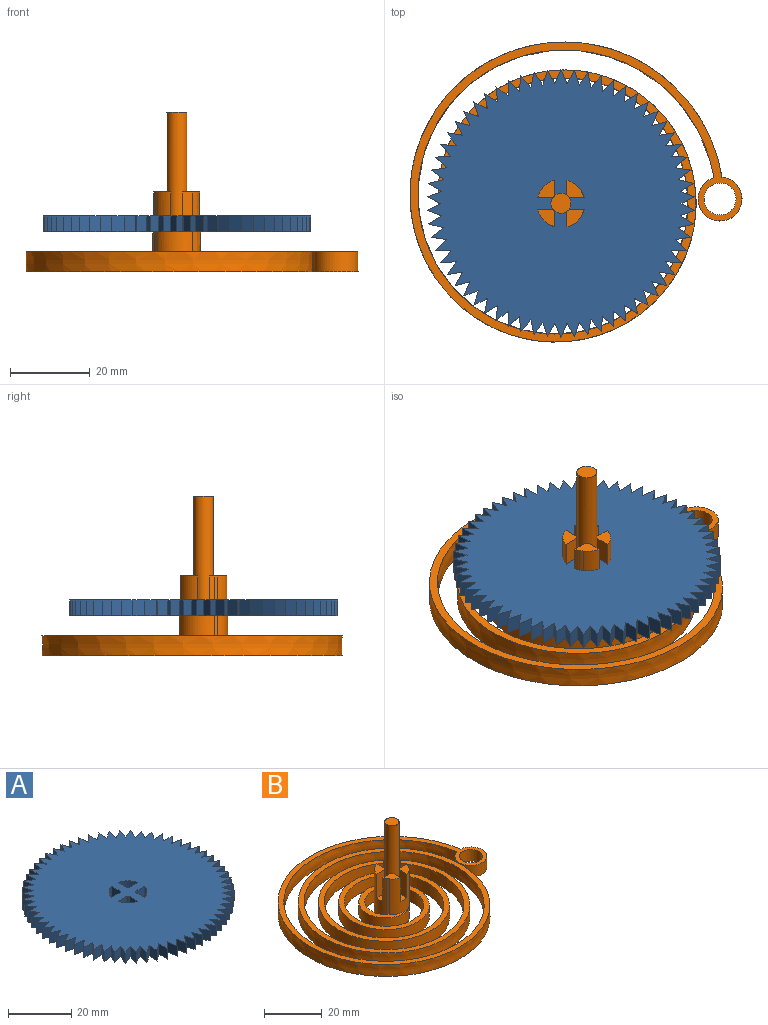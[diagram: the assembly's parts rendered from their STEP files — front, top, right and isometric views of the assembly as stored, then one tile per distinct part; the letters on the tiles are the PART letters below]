
ASSEMBLY  parts=2 mates=1
PART A: 204 faces, bbox 66.9x67x4 mm
  f0: plane 67x66.91mm, normal (0,0,1), area 3101.5mm2, adj f2,f3,f4,f5,f6,f7,f8,f9
  f1: plane 67x66.91mm, normal (0,0,-1), area 3101.5mm2, adj f2,f3,f4,f5,f6,f7,f8,f9
  f2: plane 4x3.61mm, normal (0.34,0.94,0), area 15.4mm2, adj f0,f1,f3,f187
  f3: cylinder r=30mm len=4mm, axis (0,0,-1), area 0.2mm2, adj f0,f1,f2,f4
  f4: plane 4x3.27mm, normal (0.53,-0.85,0), area 15.4mm2, adj f0,f1,f3,f5
  f5: plane 4x3.72mm, normal (0.25,0.97,0), area 15.4mm2, adj f0,f1,f4,f6
  f6: cylinder r=30mm len=4mm, axis (0,0,-1), area 0.2mm2, adj f0,f1,f5,f7
  f7: plane 4x3.05mm, normal (0.61,-0.79,0), area 15.4mm2, adj f0,f1,f6,f8
  f8: plane 4x3.8mm, normal (0.15,0.99,0), area 15.4mm2, adj f0,f1,f7,f9
  f9: cylinder r=30mm len=4mm, axis (0,0,-1), area 0.2mm2, adj f0,f1,f8,f10
  f10: plane 4x2.8mm, normal (0.69,-0.73,0), area 15.4mm2, adj f0,f1,f9,f11
  f11: plane 4x3.84mm, normal (0.05,1,0), area 15.4mm2, adj f0,f1,f10,f12
  f12: cylinder r=30mm len=4mm, axis (0,0,-1), area 0.2mm2, adj f0,f1,f11,f13
  f13: plane 4x2.9mm, normal (0.76,-0.65,0), area 15.4mm2, adj f0,f1,f12,f14
  f14: plane 4x3.84mm, normal (-0.05,1,0), area 15.4mm2, adj f0,f1,f13,f15
  f15: cylinder r=30mm len=4mm, axis (0,0,-1), area 0.2mm2, adj f0,f1,f14,f16
  f16: plane 4x3.14mm, normal (0.82,-0.57,0), area 15.4mm2, adj f0,f1,f15,f17
  f17: plane 4x3.8mm, normal (-0.16,0.99,0), area 15.4mm2, adj f0,f1,f16,f18
  f18: cylinder r=30mm len=4mm, axis (0,0,-1), area 0.2mm2, adj f0,f1,f17,f19
  f19: plane 4x3.35mm, normal (0.87,-0.49,0), area 15.4mm2, adj f0,f1,f18,f20
  f20: plane 4x3.72mm, normal (-0.25,0.97,0), area 15.4mm2, adj f0,f1,f19,f21
  f21: cylinder r=30mm len=4mm, axis (0,0,-1), area 0.2mm2, adj f0,f1,f20,f22
  f22: plane 4x3.52mm, normal (0.92,-0.4,0), area 15.4mm2, adj f0,f1,f21,f23
  f23: plane 4x3.6mm, normal (-0.35,0.94,0), area 15.4mm2, adj f0,f1,f22,f24
  f24: cylinder r=30mm len=4mm, axis (0,0,-1), area 0.2mm2, adj f0,f1,f23,f25
  f25: plane 4x3.66mm, normal (0.95,-0.3,0), area 15.4mm2, adj f0,f1,f24,f26
  f26: plane 4x3.44mm, normal (-0.44,0.9,0), area 15.4mm2, adj f0,f1,f25,f27
  f27: cylinder r=30mm len=4mm, axis (0,0,-1), area 0.2mm2, adj f0,f1,f26,f28
  f28: plane 4x3.76mm, normal (0.98,-0.21,0), area 15.4mm2, adj f0,f1,f27,f29
  f29: plane 4x3.25mm, normal (-0.53,0.85,0), area 15.4mm2, adj f0,f1,f28,f30
  f30: cylinder r=30mm len=4mm, axis (0,0,-1), area 0.2mm2, adj f0,f1,f29,f31
  f31: plane 4x3.82mm, normal (0.99,-0.11,0), area 15.4mm2, adj f0,f1,f30,f32
  f32: plane 4x3.03mm, normal (-0.62,0.79,0), area 15.4mm2, adj f0,f1,f31,f33
  f33: cylinder r=30mm len=4mm, axis (0,0,-1), area 0.2mm2, adj f0,f1,f32,f34
  f34: plane 4x3.84mm, normal (1,0,0), area 15.4mm2, adj f0,f1,f33,f35
  f35: plane 4x2.77mm, normal (-0.69,0.72,0), area 15.4mm2, adj f0,f1,f34,f36
  f36: cylinder r=30mm len=4mm, axis (0,0,-1), area 0.2mm2, adj f0,f1,f35,f37
  f37: plane 4x3.82mm, normal (1,0.1,0), area 15.4mm2, adj f0,f1,f36,f38
  f38: plane 4x2.93mm, normal (-0.76,0.65,0), area 15.4mm2, adj f0,f1,f37,f39
  f39: cylinder r=30mm len=4mm, axis (0,0,-1), area 0.2mm2, adj f0,f1,f38,f40
  f40: plane 4x3.77mm, normal (0.98,0.2,0), area 15.4mm2, adj f0,f1,f39,f41
  f41: plane 4x3.16mm, normal (-0.82,0.57,0), area 15.4mm2, adj f0,f1,f40,f42
  f42: cylinder r=30mm len=4mm, axis (0,0,-1), area 0.2mm2, adj f0,f1,f41,f43
  f43: plane 4x3.67mm, normal (0.96,0.3,0), area 15.4mm2, adj f0,f1,f42,f44
  f44: plane 4x3.37mm, normal (-0.88,0.48,0), area 15.4mm2, adj f0,f1,f43,f45
  f45: cylinder r=30mm len=4mm, axis (0,0,-1), area 0.2mm2, adj f0,f1,f44,f46
  f46: plane 4x3.54mm, normal (0.92,0.39,0), area 15.4mm2, adj f0,f1,f45,f47
  f47: plane 4x3.54mm, normal (-0.92,0.39,0), area 15.4mm2, adj f0,f1,f46,f48
  f48: cylinder r=30mm len=4mm, axis (0,0,-1), area 0.2mm2, adj f0,f1,f47,f49
  f49: plane 4x3.37mm, normal (0.88,0.48,0), area 15.4mm2, adj f0,f1,f48,f50
  f50: plane 4x3.67mm, normal (-0.96,0.3,0), area 15.4mm2, adj f0,f1,f49,f51
  f51: cylinder r=30mm len=4mm, axis (0,0,-1), area 0.2mm2, adj f0,f1,f50,f52
  f52: plane 4x3.16mm, normal (0.82,0.57,0), area 15.4mm2, adj f0,f1,f51,f53
  f53: plane 4x3.77mm, normal (-0.98,0.2,0), area 15.4mm2, adj f0,f1,f52,f54
  f54: cylinder r=30mm len=4mm, axis (0,0,-1), area 0.2mm2, adj f0,f1,f53,f55
  f55: plane 4x2.93mm, normal (0.76,0.65,0), area 15.4mm2, adj f0,f1,f54,f56
  f56: plane 4x3.82mm, normal (-1,0.1,0), area 15.4mm2, adj f0,f1,f55,f57
  f57: cylinder r=30mm len=4mm, axis (0,0,-1), area 0.2mm2, adj f0,f1,f56,f58
  f58: plane 4x2.77mm, normal (0.69,0.72,0), area 15.4mm2, adj f0,f1,f57,f59
  f59: plane 4x3.84mm, normal (-1,0,0), area 15.4mm2, adj f0,f1,f58,f60
  f60: cylinder r=30mm len=4mm, axis (0,0,-1), area 0.2mm2, adj f0,f1,f59,f61
  f61: plane 4x3.03mm, normal (0.62,0.79,0), area 15.4mm2, adj f0,f1,f60,f62
  f62: plane 4x3.82mm, normal (-0.99,-0.11,0), area 15.4mm2, adj f0,f1,f61,f63
  f63: cylinder r=30mm len=4mm, axis (0,0,-1), area 0.2mm2, adj f0,f1,f62,f64
  f64: plane 4x3.25mm, normal (0.53,0.85,0), area 15.4mm2, adj f0,f1,f63,f65
  f65: plane 4x3.76mm, normal (-0.98,-0.21,0), area 15.4mm2, adj f0,f1,f64,f66
  f66: cylinder r=30mm len=4mm, axis (0,0,-1), area 0.2mm2, adj f0,f1,f65,f67
  f67: plane 4x3.44mm, normal (0.44,0.9,0), area 15.4mm2, adj f0,f1,f66,f68
  f68: plane 4x3.66mm, normal (-0.95,-0.3,0), area 15.4mm2, adj f0,f1,f67,f69
  f69: cylinder r=30mm len=4mm, axis (0,0,-1), area 0.2mm2, adj f0,f1,f68,f70
  f70: plane 4x3.6mm, normal (0.35,0.94,0), area 15.4mm2, adj f0,f1,f69,f71
  f71: plane 4x3.52mm, normal (-0.92,-0.4,0), area 15.4mm2, adj f0,f1,f70,f72
  f72: cylinder r=30mm len=4mm, axis (0,0,-1), area 0.2mm2, adj f0,f1,f71,f73
  f73: plane 4x3.72mm, normal (0.25,0.97,0), area 15.4mm2, adj f0,f1,f72,f74
  f74: plane 4x3.35mm, normal (-0.87,-0.49,0), area 15.4mm2, adj f0,f1,f73,f75
  f75: cylinder r=30mm len=4mm, axis (0,0,-1), area 0.2mm2, adj f0,f1,f74,f76
  f76: plane 4x3.8mm, normal (0.16,0.99,0), area 15.4mm2, adj f0,f1,f75,f77
  f77: plane 4x3.14mm, normal (-0.82,-0.57,0), area 15.4mm2, adj f0,f1,f76,f78
  f78: cylinder r=30mm len=4mm, axis (0,0,-1), area 0.2mm2, adj f0,f1,f77,f79
  f79: plane 4x3.84mm, normal (0.05,1,0), area 15.4mm2, adj f0,f1,f78,f80
  f80: plane 4x2.9mm, normal (-0.76,-0.65,0), area 15.4mm2, adj f0,f1,f79,f81
  f81: cylinder r=30mm len=4mm, axis (0,0,-1), area 0.2mm2, adj f0,f1,f80,f82
  f82: plane 4x3.84mm, normal (-0.05,1,0), area 15.4mm2, adj f0,f1,f81,f83
  f83: plane 4x2.8mm, normal (-0.69,-0.73,0), area 15.4mm2, adj f0,f1,f82,f84
  f84: cylinder r=30mm len=4mm, axis (0,0,-1), area 0.2mm2, adj f0,f1,f83,f85
  f85: plane 4x3.8mm, normal (-0.15,0.99,0), area 15.4mm2, adj f0,f1,f84,f86
  f86: plane 4x3.05mm, normal (-0.61,-0.79,0), area 15.4mm2, adj f0,f1,f85,f87
  f87: cylinder r=30mm len=4mm, axis (0,0,-1), area 0.2mm2, adj f0,f1,f86,f88
  f88: plane 4x3.72mm, normal (-0.25,0.97,0), area 15.4mm2, adj f0,f1,f87,f89
  f89: plane 4x3.27mm, normal (-0.53,-0.85,0), area 15.4mm2, adj f0,f1,f88,f90
  f90: cylinder r=30mm len=4mm, axis (0,0,-1), area 0.2mm2, adj f0,f1,f89,f91
  f91: plane 4x3.61mm, normal (-0.34,0.94,0), area 15.4mm2, adj f0,f1,f90,f92
  f92: plane 4x3.46mm, normal (-0.44,-0.9,0), area 15.4mm2, adj f0,f1,f91,f93
  f93: cylinder r=30mm len=4mm, axis (0,0,-1), area 0.2mm2, adj f0,f1,f92,f94
  f94: plane 4x3.46mm, normal (-0.44,0.9,0), area 15.4mm2, adj f0,f1,f93,f95
  f95: plane 4x3.61mm, normal (-0.34,-0.94,0), area 15.4mm2, adj f0,f1,f94,f96
  f96: cylinder r=30mm len=4mm, axis (0,0,-1), area 0.2mm2, adj f0,f1,f95,f97
  f97: plane 4x3.27mm, normal (-0.53,0.85,0), area 15.4mm2, adj f0,f1,f96,f98
  f98: plane 4x3.72mm, normal (-0.25,-0.97,0), area 15.4mm2, adj f0,f1,f97,f99
  f99: cylinder r=30mm len=4mm, axis (0,0,-1), area 0.2mm2, adj f0,f1,f98,f100
  f100: plane 4x3.05mm, normal (-0.61,0.79,0), area 15.4mm2, adj f0,f1,f99,f101
  f101: plane 4x3.8mm, normal (-0.15,-0.99,0), area 15.4mm2, adj f0,f1,f100,f102
  f102: cylinder r=30mm len=4mm, axis (0,0,-1), area 0.2mm2, adj f0,f1,f101,f103
  f103: plane 4x2.8mm, normal (-0.69,0.73,0), area 15.4mm2, adj f0,f1,f102,f104
  f104: plane 4x3.84mm, normal (-0.05,-1,0), area 15.4mm2, adj f0,f1,f103,f105
  f105: cylinder r=30mm len=4mm, axis (0,0,-1), area 0.2mm2, adj f0,f1,f104,f106
  f106: plane 4x2.9mm, normal (-0.76,0.65,0), area 15.4mm2, adj f0,f1,f105,f107
  f107: plane 4x3.84mm, normal (0.05,-1,0), area 15.4mm2, adj f0,f1,f106,f108
  f108: cylinder r=30mm len=4mm, axis (0,0,-1), area 0.2mm2, adj f0,f1,f107,f109
  f109: plane 4x3.14mm, normal (-0.82,0.57,0), area 15.4mm2, adj f0,f1,f108,f110
  f110: plane 4x3.8mm, normal (0.16,-0.99,0), area 15.4mm2, adj f0,f1,f109,f111
  f111: cylinder r=30mm len=4mm, axis (0,0,-1), area 0.2mm2, adj f0,f1,f110,f112
  f112: plane 4x3.35mm, normal (-0.87,0.49,0), area 15.4mm2, adj f0,f1,f111,f113
  f113: plane 4x3.72mm, normal (0.25,-0.97,0), area 15.4mm2, adj f0,f1,f112,f114
  f114: cylinder r=30mm len=4mm, axis (0,0,-1), area 0.2mm2, adj f0,f1,f113,f115
  f115: plane 4x3.52mm, normal (-0.92,0.4,0), area 15.4mm2, adj f0,f1,f114,f116
  f116: plane 4x3.6mm, normal (0.35,-0.94,0), area 15.4mm2, adj f0,f1,f115,f117
  f117: cylinder r=30mm len=4mm, axis (0,0,-1), area 0.2mm2, adj f0,f1,f116,f118
  f118: plane 4x3.66mm, normal (-0.95,0.3,0), area 15.4mm2, adj f0,f1,f117,f119
  f119: plane 4x3.44mm, normal (0.44,-0.9,0), area 15.4mm2, adj f0,f1,f118,f120
  f120: cylinder r=30mm len=4mm, axis (0,0,-1), area 0.2mm2, adj f0,f1,f119,f121
  f121: plane 4x3.76mm, normal (-0.98,0.21,0), area 15.4mm2, adj f0,f1,f120,f122
  f122: plane 4x3.25mm, normal (0.53,-0.85,0), area 15.4mm2, adj f0,f1,f121,f123
  f123: cylinder r=30mm len=4mm, axis (0,0,-1), area 0.2mm2, adj f0,f1,f122,f124
  f124: plane 4x3.82mm, normal (-0.99,0.11,0), area 15.4mm2, adj f0,f1,f123,f125
  f125: plane 4x3.03mm, normal (0.62,-0.79,0), area 15.4mm2, adj f0,f1,f124,f126
  f126: cylinder r=30mm len=4mm, axis (0,0,-1), area 0.2mm2, adj f0,f1,f125,f127
  f127: plane 4x3.84mm, normal (-1,0,0), area 15.4mm2, adj f0,f1,f126,f128
  f128: plane 4x2.77mm, normal (0.69,-0.72,0), area 15.4mm2, adj f0,f1,f127,f129
  f129: cylinder r=30mm len=4mm, axis (0,0,-1), area 0.2mm2, adj f0,f1,f128,f130
  f130: plane 4x3.82mm, normal (-1,-0.1,0), area 15.4mm2, adj f0,f1,f129,f131
  f131: plane 4x2.93mm, normal (0.76,-0.65,0), area 15.4mm2, adj f0,f1,f130,f132
  f132: cylinder r=30mm len=4mm, axis (0,0,-1), area 0.2mm2, adj f0,f1,f131,f133
  f133: plane 4x3.77mm, normal (-0.98,-0.2,0), area 15.4mm2, adj f0,f1,f132,f134
  f134: plane 4x3.16mm, normal (0.82,-0.57,0), area 15.4mm2, adj f0,f1,f133,f135
  f135: cylinder r=30mm len=4mm, axis (0,0,-1), area 0.2mm2, adj f0,f1,f134,f136
  f136: plane 4x3.67mm, normal (-0.96,-0.3,0), area 15.4mm2, adj f0,f1,f135,f137
  f137: plane 4x3.37mm, normal (0.88,-0.48,0), area 15.4mm2, adj f0,f1,f136,f138
  f138: cylinder r=30mm len=4mm, axis (0,0,-1), area 0.2mm2, adj f0,f1,f137,f139
  f139: plane 4x3.54mm, normal (-0.92,-0.39,0), area 15.4mm2, adj f0,f1,f138,f140
  f140: plane 4x3.54mm, normal (0.92,-0.39,0), area 15.4mm2, adj f0,f1,f139,f141
  f141: cylinder r=30mm len=4mm, axis (0,0,-1), area 0.2mm2, adj f0,f1,f140,f142
  f142: plane 4x3.37mm, normal (-0.88,-0.48,0), area 15.4mm2, adj f0,f1,f141,f143
  f143: plane 4x3.67mm, normal (0.96,-0.3,0), area 15.4mm2, adj f0,f1,f142,f144
  f144: cylinder r=30mm len=4mm, axis (0,0,-1), area 0.2mm2, adj f0,f1,f143,f145
  f145: plane 4x3.16mm, normal (-0.82,-0.57,0), area 15.4mm2, adj f0,f1,f144,f146
  f146: plane 4x3.77mm, normal (0.98,-0.2,0), area 15.4mm2, adj f0,f1,f145,f147
  f147: cylinder r=30mm len=4mm, axis (0,0,-1), area 0.2mm2, adj f0,f1,f146,f148
  f148: plane 4x2.93mm, normal (-0.76,-0.65,0), area 15.4mm2, adj f0,f1,f147,f149
  f149: plane 4x3.82mm, normal (1,-0.1,0), area 15.4mm2, adj f0,f1,f148,f150
  f150: cylinder r=30mm len=4mm, axis (0,0,-1), area 0.2mm2, adj f0,f1,f149,f151
  f151: plane 4x2.77mm, normal (-0.69,-0.72,0), area 15.4mm2, adj f0,f1,f150,f152
  f152: plane 4x3.84mm, normal (1,0,0), area 15.4mm2, adj f0,f1,f151,f153
  f153: cylinder r=30mm len=4mm, axis (0,0,-1), area 0.2mm2, adj f0,f1,f152,f154
  f154: plane 4x3.03mm, normal (-0.62,-0.79,0), area 15.4mm2, adj f0,f1,f153,f155
  f155: plane 4x3.82mm, normal (0.99,0.11,0), area 15.4mm2, adj f0,f1,f154,f156
  f156: cylinder r=30mm len=4mm, axis (0,0,-1), area 0.2mm2, adj f0,f1,f155,f157
  f157: plane 4x3.25mm, normal (-0.53,-0.85,0), area 15.4mm2, adj f0,f1,f156,f158
  f158: plane 4x3.76mm, normal (0.98,0.21,0), area 15.4mm2, adj f0,f1,f157,f159
  f159: cylinder r=30mm len=4mm, axis (0,0,-1), area 0.2mm2, adj f0,f1,f158,f160
  f160: plane 4x3.44mm, normal (-0.44,-0.9,0), area 15.4mm2, adj f0,f1,f159,f161
  f161: plane 4x3.66mm, normal (0.95,0.3,0), area 15.4mm2, adj f0,f1,f160,f162
  f162: cylinder r=30mm len=4mm, axis (0,0,-1), area 0.2mm2, adj f0,f1,f161,f163
  f163: plane 4x3.6mm, normal (-0.35,-0.94,0), area 15.4mm2, adj f0,f1,f162,f164
  f164: plane 4x3.52mm, normal (0.92,0.4,0), area 15.4mm2, adj f0,f1,f163,f165
  f165: cylinder r=30mm len=4mm, axis (0,0,-1), area 0.2mm2, adj f0,f1,f164,f166
  f166: plane 4x3.72mm, normal (-0.25,-0.97,0), area 15.4mm2, adj f0,f1,f165,f167
  f167: plane 4x3.35mm, normal (0.87,0.49,0), area 15.4mm2, adj f0,f1,f166,f168
  f168: cylinder r=30mm len=4mm, axis (0,0,-1), area 0.2mm2, adj f0,f1,f167,f169
  f169: plane 4x3.8mm, normal (-0.16,-0.99,0), area 15.4mm2, adj f0,f1,f168,f170
  f170: plane 4x3.14mm, normal (0.82,0.57,0), area 15.4mm2, adj f0,f1,f169,f171
  f171: cylinder r=30mm len=4mm, axis (0,0,-1), area 0.2mm2, adj f0,f1,f170,f172
  f172: plane 4x3.84mm, normal (-0.05,-1,0), area 15.4mm2, adj f0,f1,f171,f173
  f173: plane 4x2.9mm, normal (0.76,0.65,0), area 15.4mm2, adj f0,f1,f172,f174
  f174: cylinder r=30mm len=4mm, axis (0,0,-1), area 0.2mm2, adj f0,f1,f173,f175
  f175: plane 4x3.84mm, normal (0.05,-1,0), area 15.4mm2, adj f0,f1,f174,f176
  f176: plane 4x2.8mm, normal (0.69,0.73,0), area 15.4mm2, adj f0,f1,f175,f177
  f177: cylinder r=30mm len=4mm, axis (0,0,-1), area 0.2mm2, adj f0,f1,f176,f178
  f178: plane 4x3.8mm, normal (0.15,-0.99,0), area 15.4mm2, adj f0,f1,f177,f179
  f179: plane 4x3.05mm, normal (0.61,0.79,0), area 15.4mm2, adj f0,f1,f178,f180
  f180: cylinder r=30mm len=4mm, axis (0,0,-1), area 0.2mm2, adj f0,f1,f179,f181
  f181: plane 4x3.72mm, normal (0.25,-0.97,0), area 15.4mm2, adj f0,f1,f180,f182
  f182: plane 4x3.27mm, normal (0.53,0.85,0), area 15.4mm2, adj f0,f1,f181,f183
  f183: cylinder r=30mm len=4mm, axis (0,0,-1), area 0.2mm2, adj f0,f1,f182,f184
  f184: plane 4x3.61mm, normal (0.34,-0.94,0), area 15.4mm2, adj f0,f1,f183,f185
  f185: plane 4x3.46mm, normal (0.44,0.9,0), area 15.4mm2, adj f0,f1,f184,f186
  f186: cylinder r=30mm len=4mm, axis (0,0,-1), area 0.2mm2, adj f0,f1,f185,f187
  f187: plane 4x3.46mm, normal (0.44,-0.9,0), area 15.4mm2, adj f0,f1,f2,f186
  f188: plane 4x3.81mm, normal (0,1,0), area 15.2mm2, adj f0,f1,f189,f191
  f189: cylinder r=2.5mm len=4mm, axis (0,0,1), area 2.8mm2, adj f0,f1,f188,f190
  f190: plane 4x3.81mm, normal (-1,0,0), area 15.2mm2, adj f0,f1,f189,f191
  f191: cylinder r=6mm len=4.31mm, axis (0,0,1), area 25.6mm2, adj f0,f1,f188,f190
  f192: plane 4x3.81mm, normal (0,1,0), area 15.2mm2, adj f0,f1,f193,f195
  f193: cylinder r=6mm len=4.31mm, axis (0,0,1), area 25.6mm2, adj f0,f1,f192,f194
  f194: plane 4x3.81mm, normal (1,0,0), area 15.2mm2, adj f0,f1,f193,f195
  f195: cylinder r=2.5mm len=4mm, axis (0,0,1), area 2.8mm2, adj f0,f1,f192,f194
  f196: plane 4x3.81mm, normal (1,0,0), area 15.2mm2, adj f0,f1,f197,f199
  f197: cylinder r=6mm len=4.31mm, axis (0,0,1), area 25.6mm2, adj f0,f1,f196,f198
  f198: plane 4x3.81mm, normal (0,-1,0), area 15.2mm2, adj f0,f1,f197,f199
  f199: cylinder r=2.5mm len=4mm, axis (0,0,1), area 2.8mm2, adj f0,f1,f196,f198
  f200: plane 4x3.81mm, normal (-1,0,0), area 15.2mm2, adj f0,f1,f201,f203
  f201: cylinder r=2.5mm len=4mm, axis (0,0,1), area 2.8mm2, adj f0,f1,f200,f202
  f202: plane 4x3.81mm, normal (0,-1,0), area 15.2mm2, adj f0,f1,f201,f203
  f203: cylinder r=6mm len=4.31mm, axis (0,0,1), area 25.6mm2, adj f0,f1,f200,f202
PART B: 30 faces, bbox 83.2x75.3x40 mm
  f0: extruded ~77.64x70.27mm, area 3637.6mm2, adj f1,f9,f11,f14
  f1: extruded ~20x6.07mm, area 104.5mm2, adj f0,f3,f4,f6,f11,f21,f22
  f2: cylinder r=6.04mm len=15mm, axis (0,0,-1), area 139.3mm2, adj f4,f5,f7,f10,f18,f19,f27,f28
  f3: cylinder r=6.04mm len=15mm, axis (0,0,-1), area 116.1mm2, adj f1,f5,f6,f8,f9,f24,f25,f26
  f4: cylinder r=5.98mm len=20mm, axis (0,0,1), area 225.4mm2, adj f1,f2,f5,f8,f10,f11,f12,f16
  f5: plane 4.35x4.35mm, normal (0,0,1), area 12.8mm2, adj f2,f3,f4,f8,f15,f26,f28
  f6: plane 4.37x4.21mm, normal (0,0,1), area 12.4mm2, adj f1,f3,f15,f22,f25
  f7: plane 4.35x4.35mm, normal (0,0,1), area 12.8mm2, adj f2,f15,f19,f29
  f8: extruded ~15x0.04mm, area 0.7mm2, adj f3,f4,f5,f12
  f9: plane 83.12x75.18mm, normal (0,0,1), area 1412.2mm2, adj f0,f3,f12,f13,f14
  f10: plane 8.83x5.84mm, normal (0,0,1), area 0.4mm2, adj f2,f4
  f11: plane 83.16x75.25mm, normal (0,0,-1), area 1527.4mm2, adj f0,f1,f4,f12,f13,f14
  f12: extruded ~72.81x68.03mm, area 3293.5mm2, adj f4,f8,f9,f11,f14
  f13: cylinder r=4mm len=8mm, axis (0,0,1), area 125.7mm2, adj f9,f11
  f14: cylinder r=5.5mm len=11mm, axis (0,0,1), area 162.7mm2, adj f0,f9,f11,f12
  f15: cylinder r=2.5mm len=30mm, axis (0,0,1), area 442.9mm2, adj f5,f6,f7,f16,f17,f18,f19,f20
  f16: plane 4.32x4.21mm, normal (0,0,1), area 12.3mm2, adj f4,f15,f20,f23
  f17: plane 5x5mm, normal (0,0,1), area 19.6mm2, adj f15
  f18: plane 4.04x3mm, normal (0,0,1), area 10.9mm2, adj f2,f4,f15,f19,f20
  f19: plane 10x3.85mm, normal (1,0,0), area 38.5mm2, adj f2,f7,f15,f18
  f20: plane 10x3.82mm, normal (-1,0,0), area 38.2mm2, adj f4,f15,f16,f18
  f21: plane 3.9x3.02mm, normal (0,0,1), area 10.4mm2, adj f1,f4,f15,f22,f23
  f22: plane 10x3.69mm, normal (0,1,0), area 36.9mm2, adj f1,f6,f15,f21
  f23: plane 10x3.71mm, normal (0,-1,0), area 37.1mm2, adj f4,f15,f16,f21
  f24: plane 4.04x3mm, normal (0,0,1), area 10.9mm2, adj f3,f15,f25,f26
  f25: plane 10x3.85mm, normal (-1,0,0), area 38.5mm2, adj f3,f6,f15,f24
  f26: plane 10x3.85mm, normal (1,0,0), area 38.5mm2, adj f3,f5,f15,f24
  f27: plane 4.04x3mm, normal (0,0,1), area 10.9mm2, adj f2,f15,f28,f29
  f28: plane 10x3.85mm, normal (0,1,0), area 38.5mm2, adj f2,f5,f15,f27
  f29: plane 10x3.85mm, normal (0,-1,0), area 38.5mm2, adj f2,f7,f15,f27
PLACE A t=(-13.54,-42.85,-32.86)mm
PLACE B t=(-13.77,-41.67,-42.86)mm
MATE fastened A.f1 <-> B.f24  axis (0,0,-1) through (-12.04,-48.66,-32.86)mm
